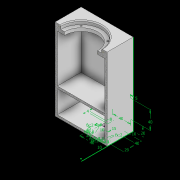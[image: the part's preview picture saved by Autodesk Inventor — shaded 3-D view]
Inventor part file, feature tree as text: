
AUTODESK INVENTOR PART (.ipt)
format: ipt  version: 2022 (Build 260153000, 153)  size: 329,216 bytes
history: native  units: in
note: dims shown in document units (in); Inventor stores cm internally (conversion verified against a paired STEP export)
features: extrude x17, sketch x16, projected_geometry x3, plane x1, split x1, chamfer x1
ambient origin geometry x8: Origin, YZ Plane, XZ Plane, XY Plane, X Axis, Y Axis, Z Axis, Center Point
bodies: Solid1 (feature_tree)
feature tree (39):
  extrude  "Extrusion1"  Depth=4.1339in
  extrude  "Extrusion2"  Depth=2.0669in
  extrude  "Extrusion3"  Depth=0.2756in TaperAngle=0.0deg
  extrude  "Extrusion4"  Depth=0.1969in TaperAngle=0.0deg
  extrude  "Extrusion5"  Depth=0.1969in TaperAngle=0.0deg
  extrude  "Extrusion6"  Depth=0.1969in TaperAngle=0.0deg
  extrude  "Extrusion7"  Depth=0.315in TaperAngle=0.0deg
  extrude  "Extrusion8"  Depth=3.2874in
  plane  "Work Plane1"
  split  "Split2"
  chamfer  "Chamfer1"  Distance=0.1969in
  extrude  "Extrusion11"  Depth=0.1181in TaperAngle=0.0deg
  extrude  "Extrusion14"  Depth=1.8701in
  extrude  "Extrusion15"  Depth=0.3937in TaperAngle=0.0deg
  extrude  "Extrusion16"  Depth=1.9685in
  extrude  "Extrusion17"  Depth=0.1969in TaperAngle=0.0deg
  extrude  "Extrusion18"  Depth=0.1969in TaperAngle=0.0deg
  extrude  "Extrusion19"  Depth=0.1969in TaperAngle=0.0deg
  sketch  "Sketch25"  dims[d55=0.1575in d56=0.3937in d57=0.0in]
  extrude  "Extrusion23"  Depth=0.1969in TaperAngle=0.0deg
  extrude  "Extrusion24"  Depth=0.1969in TaperAngle=0.0deg
  sketch  "Sketch26"  dims[d58=0.0591in d59=1.9685in d60=0.1969in d61=0.0in d62=0.1969in d63=0.0in d64=0.1969in d65=0.0in d66=0.1969in d67=0.0in d68=0.1969in d69=0.0in d101=1.5748in d102=1.5748in d103=0.1496in d104=0.1496in d105=0.1496in d106=0.1496in d107=0.1575in d108=0.0787in d109=0.0787in d110=0.1575in d111=0.9843in d112=0.0787in d113=1.1417in d114=0.0787in d115=0.0787in d116=0.0787in d117=0.0787in d118=0.0787in d119=0.1181in d120=0.0in d124=0.3937in d125=0.3937in d126=0.3937in d127=0.5906in d128=0.1575in d129=0.315in d130=0.1181in d131=0.1969in d132=0.0in d133=0.0in d134=0.1575in d135=0.1575in d136=0.315in d137=0.315in d142=1.5748in d143=1.5748in d144=0.7874in d145=0.1969in d33=0.0197in d34=0.0344in d35=0.0197in d36=0.0344in d44=0.0344in d46=0.0197in d49=0.0344in d138=0.0197in d139=0.0344in d140=0.0197in d141=0.0344in]
  sketch  "Sketch1"  dims[d0=4.1339in d1=4.1339in]
  sketch  "Sketch3"  dims[d2=2.0669in d3=2.0669in]
  sketch  "Sketch4"  dims[d4=2.874in d5=0.2756in d6=0.0in]
  sketch  "Sketch6"  dims[d7=4.1339in d8=0.1969in d9=0.0in]
  sketch  "Sketch7"  dims[d10=0.1969in d11=0.0in d12=0.1969in d13=0.0in]
  sketch  "Sketch8"  dims[d14=0.1969in d15=0.0in d16=0.1969in d17=0.0in]
  sketch  "Sketch9"  dims[d18=3.5433in d19=0.315in d20=0.0in]
  projected_geometry  "Projected Loop1"
  sketch  "Sketch10"  dims[d21=0.1496in d22=3.2874in]
  sketch  "Sketch16"  dims[d23=0.1496in]
  projected_geometry  "Projected Loop4"
  sketch  "Sketch17"  dims[d24=0.1496in]
  sketch  "Sketch18"  dims[d25=0.1496in]
  sketch  "Sketch19"  dims[d26=45.0deg d27=0.1969in d28=0.0in]
  sketch  "Sketch20"  dims[d41=0.0787in d42=0.0787in d43=45.0deg d47=0.1181in d48=0.0in]
  sketch  "Sketch21"  dims[d53=3.7402in d54=1.8701in]
  projected_geometry  "Project Cut Edges3"
